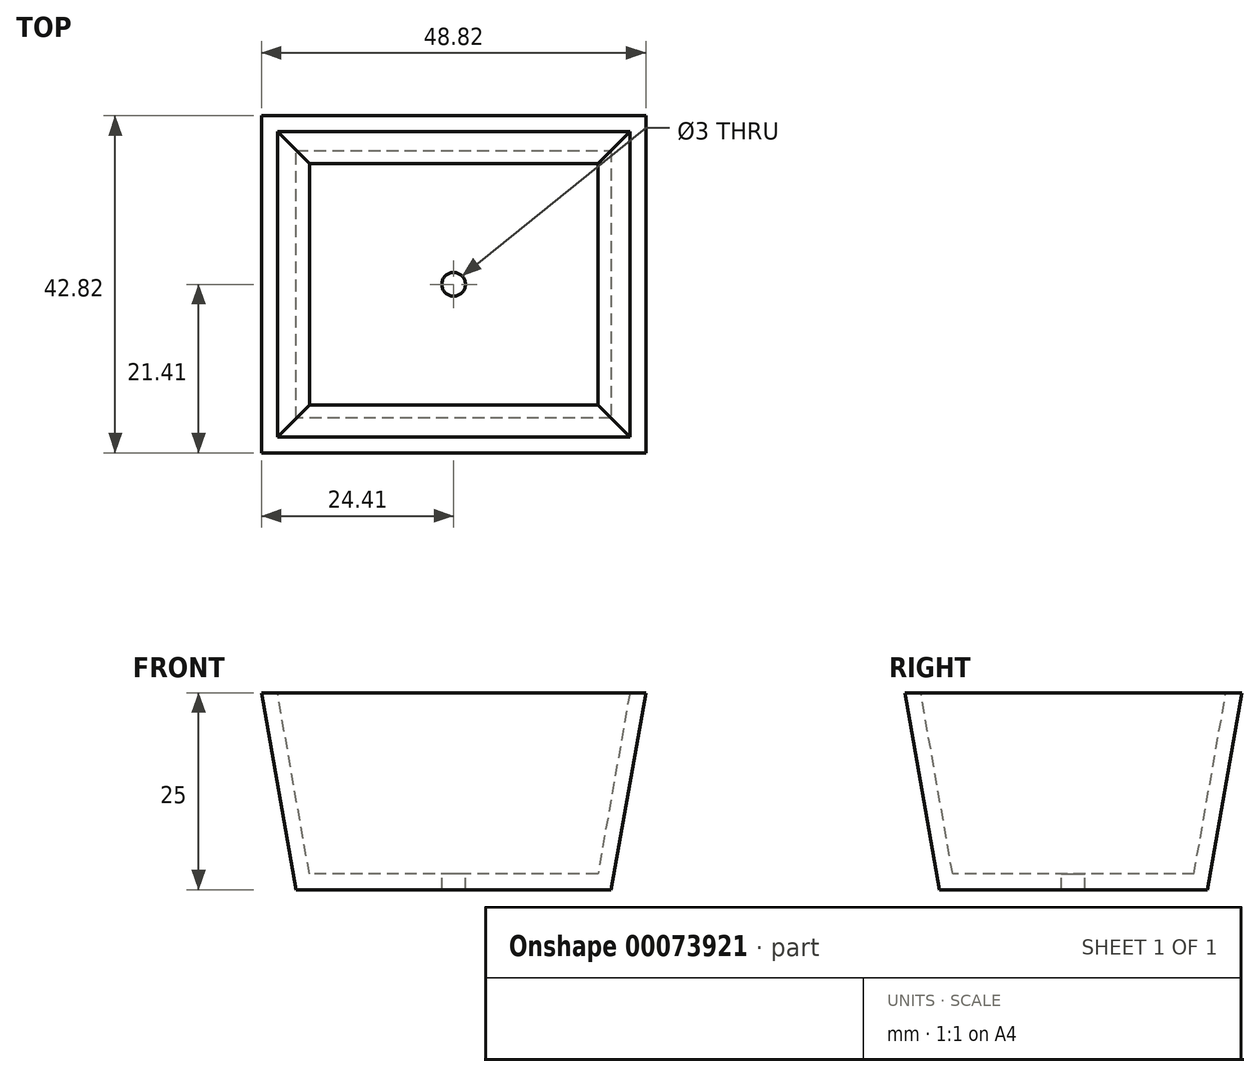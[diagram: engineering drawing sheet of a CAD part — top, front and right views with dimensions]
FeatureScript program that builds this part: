
annotation { "Feature Type Name" : "Feature", "Feature Type Description" : "" }
export const myFeature = defineFeature(function(context is Context, id is Id, definition is map)
    precondition{}
    {
        {
            var Q0;
            Q0=qCreatedBy(makeId("Top.planeOp"),FACE);
            var sketch = newSketch(context, id + "F0", { "sketchPlane" : qUnion([Q0])});
            skLineSegment(sketch, "E0.bottom", {"start": v(0, 0) * mm, "end": v(40, 0) * mm});
            skLineSegment(sketch, "E0.top", {"start": v(0, 34) * mm, "end": v(40, 34) * mm});
            skLineSegment(sketch, "E0.left", {"start": v(0, 0) * mm, "end": v(0, 34) * mm});
            skLineSegment(sketch, "E0.right", {"start": v(40, 0) * mm, "end": v(40, 34) * mm});
            skLineSegment(sketch, "E1", {"start": v(0, 34) * mm, "end": v(8, 34) * mm, "construction": true});
            skLineSegment(sketch, "E2", {"start": v(40, 34) * mm, "end": v(32, 34) * mm, "construction": true});
            skLineSegment(sketch, "E3", {"start": v(8, 34) * mm, "end": v(8, 35) * mm});
            skLineSegment(sketch, "E4", {"start": v(8, 35) * mm, "end": v(13, 35) * mm});
            skLineSegment(sketch, "E5", {"start": v(13, 35) * mm, "end": v(13, 34) * mm});
            skLineSegment(sketch, "E6", {"start": v(32, 34) * mm, "end": v(32, 35) * mm});
            skLineSegment(sketch, "E7", {"start": v(32, 35) * mm, "end": v(27, 35) * mm});
            skLineSegment(sketch, "E8", {"start": v(27, 35) * mm, "end": v(27, 34) * mm});
            skLineSegment(sketch, "E9", {"start": v(8, 0) * mm, "end": v(8, -1) * mm});
            skLineSegment(sketch, "E10", {"start": v(8, -1) * mm, "end": v(13, -1) * mm});
            skLineSegment(sketch, "E11", {"start": v(13, -1) * mm, "end": v(13, 0) * mm});
            skLineSegment(sketch, "E12", {"start": v(27, 0) * mm, "end": v(27, -1) * mm});
            skLineSegment(sketch, "E13", {"start": v(27, -1) * mm, "end": v(32, -1) * mm});
            skLineSegment(sketch, "E14", {"start": v(32, -1) * mm, "end": v(32, 0) * mm});
            skLineSegment(sketch, "E15", {"start": v(0, 17) * mm, "end": v(0, 21) * mm, "construction": true});
            skLineSegment(sketch, "E16", {"start": v(0, 21) * mm, "end": v(-1, 21) * mm});
            skLineSegment(sketch, "E17", {"start": v(-1, 21) * mm, "end": v(-1, 13) * mm});
            skLineSegment(sketch, "E18", {"start": v(-1, 13) * mm, "end": v(0, 13) * mm});
            skLineSegment(sketch, "E19", {"start": v(40, 21) * mm, "end": v(41, 21) * mm});
            skLineSegment(sketch, "E20", {"start": v(41, 21) * mm, "end": v(41, 13) * mm});
            skLineSegment(sketch, "E21", {"start": v(41, 13) * mm, "end": v(40, 13) * mm});
            skSolve(sketch);
        }
        {
            var Q0;
            {var subQ3=sQuery(id+"F0.wireOp",EDGE,"E0.left");var subQ4=sQuery(id+"F0.wireOp",EDGE,"E0.bottom");var subQ5=makeQuery(id+"F0.imprint","INTERSECT",VERTEX,{"derivedFrom":[subQ4,subQ3]});Q0=makeQuery(id+"F0.imprint","IMPRINT",FACE,{"disambiguationData":[TD([[makeQuery(id+"F0.imprint","IMPRINT",EDGE,{"disambiguationData":[TD([[subQ5,-1.0]])],"derivedFrom":subQ4}),1.0]])]});}
            extrude(context, id + "F1", {"entities" : qUnion([Q0]), "depth" : 25 * mm, "hasDraft" : true, "draftAngle" : 10 * degree});
        }
        {
            var Q0;
            Q0=makeQuery(id+"F1.opExtrude","CAP_FACE",FACE,{"disambiguationData":[OSD([sQuery(id+"F0.wireOp",EDGE,"E0.bottom"),sQuery(id+"F0.wireOp",EDGE,"E0.top"),sQuery(id+"F0.wireOp",EDGE,"E0.left"),sQuery(id+"F0.wireOp",EDGE,"E0.right")])],"isStart":false});
            shell(context, id + "F2", {"entities" : qUnion([Q0]), "thickness" : 2 * mm});
        }
        {
            var Q0;
            Q0=makeQuery(id+"F2.opShell","OFFSET_FACE",FACE,{"disambiguationData":[OSD([sQuery(id+"F0.wireOp",EDGE,"E0.bottom"),sQuery(id+"F0.wireOp",EDGE,"E0.top"),sQuery(id+"F0.wireOp",EDGE,"E0.left"),sQuery(id+"F0.wireOp",EDGE,"E0.right")])]});
            var sketch = newSketch(context, id + "F3", { "sketchPlane" : qUnion([Q0])});
            skLineSegment(sketch, "E22", {"start": v(1.68, 32.32) * mm, "end": v(38.32, 1.68) * mm, "construction": true});
            skCircle(sketch, "E23", {"center": v(20, 17) * mm, "radius": 1.5 * mm});
            skSolve(sketch);
        }
        {
            var Q0;
            Q0 = qSketchRegion(id + "F3", true);
            extrude(context, id + "F4", {"entities" : qUnion([Q0]), "operationType" : NewBodyOperationType.REMOVE, "oppositeDirection" : true, "depth" : 25 * mm});
        }
    });
